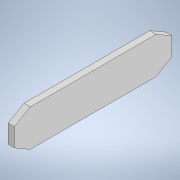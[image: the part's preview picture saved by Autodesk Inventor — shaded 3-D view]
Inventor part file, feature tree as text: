
AUTODESK INVENTOR PART (.ipt)
format: ipt  version: 2020 (Build 240168000, 168)  size: 105,984 bytes
history: native  units: in
note: dims shown in document units (in); Inventor stores cm internally (conversion verified against a paired STEP export)
features: extrude x1, sketch x1
ambient origin geometry x8: Origin, YZ Plane, XZ Plane, XY Plane, X Axis, Y Axis, Z Axis, Center Point
bodies: Solid1 (feature_tree)
feature tree (2):
  extrude  "Extrusion1"  Depth=5.9055in
  sketch  "Sketch1"  dims[d0=1.378in d1=5.9055in d2=0.2362in d3=0.0in]
